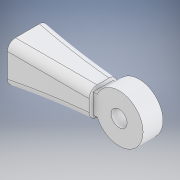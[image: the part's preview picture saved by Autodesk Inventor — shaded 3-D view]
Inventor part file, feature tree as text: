
AUTODESK INVENTOR PART (.ipt)
format: ipt  version: 2017 SP1 (Build 210196100, 196)  size: 198,656 bytes
history: native  units: in
note: dims shown in document units (in); Inventor stores cm internally (conversion verified against a paired STEP export)
features: extrude x7, sketch x7, projected_geometry x3, plane x1, fillet x1
ambient origin geometry x8: Origin, YZ Plane, XZ Plane, XY Plane, X Axis, Y Axis, Z Axis, Center Point
bodies: Solid1 (feature_tree)
feature tree (19):
  extrude  "Extrusion1"  Depth=0.4724in
  plane  "Work Plane1"
  extrude  "Extrusion2"  [1 undecoded]
  extrude  "Extrusion3"  Depth=0.1969in
  extrude  "Extrusion4"  Depth=0.6693in TaperAngle=0.0deg
  extrude  "Extrusion5"  Depth=0.3937in
  extrude  "Extrusion6"  Depth=11.811in
  fillet  "Fillet1"  Radius=11.811in
  extrude  "Extrusion7"  Depth=0.3937in
  sketch  "Sketch1"  dims[d0=0.1575in d1=0.4724in]
  sketch  "Sketch5"  dims[d2=0.1969in d3=0.0in d4=-0.0984in]
  sketch  "Sketch7"  dims[d5=0.1969in d6=0.1969in]
  projected_geometry  "Projected Loop2"
  sketch  "Sketch8"  dims[d7=0.2362in d8=0.0in d9=0.6693in d10=0.0in]
  sketch  "Sketch9"  dims[d11=0.3937in d12=0.2756in]
  sketch  "Sketch10"  dims[d13=0.2559in d14=11.811in d15=11.811in]
  projected_geometry  "Projected Loop3"
  projected_geometry  "Projected Loop4"
  sketch  "Sketch11"  dims[d16=0.2362in d17=0.0394in d18=0.0in d19=0.0in d20=0.3937in d21=11.811in d22=11.811in d23=0.0984in d24=0.2953in d25=0.0in d26=0.0in d27=0.0984in d28=0.0in d29=0.0787in d30=0.1181in d31=0.3937in d32=0.0in]
note: 1 required parameter value undecoded (feature->parameter linkage not recoverable at this tier; creation-order binding heuristic only, values carry confidence <= 0.55)
